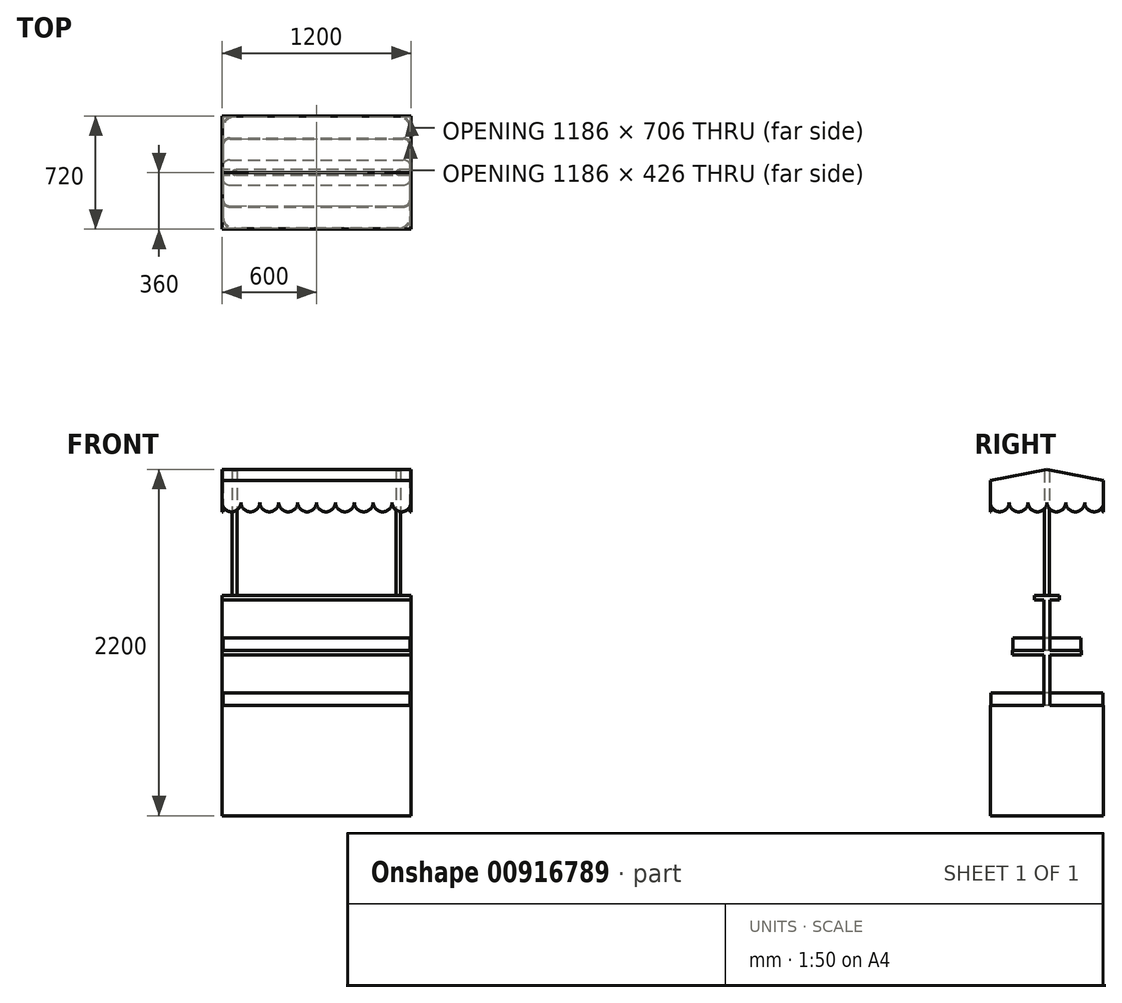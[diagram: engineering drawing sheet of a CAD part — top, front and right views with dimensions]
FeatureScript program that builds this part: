
annotation { "Feature Type Name" : "Feature", "Feature Type Description" : "" }
export const myFeature = defineFeature(function(context is Context, id is Id, definition is map)
    precondition{}
    {
        {
            var Q0;
            Q0=qCreatedBy(makeId("Front.planeOp"),FACE);
            var sketch = newSketch(context, id + "F0", { "sketchPlane" : qUnion([Q0])});
            skLineSegment(sketch, "E0.bottom", {"start": v(-600, 0) * mm, "end": v(600, 0) * mm});
            skLineSegment(sketch, "E0.top", {"start": v(-600, 1400) * mm, "end": v(600, 1400) * mm});
            skLineSegment(sketch, "E0.left", {"start": v(-600, 0) * mm, "end": v(-600, 1400) * mm});
            skLineSegment(sketch, "E0.right", {"start": v(600, 0) * mm, "end": v(600, 1400) * mm});
            skLineSegment(sketch, "E1", {"start": v(-600, 150) * mm, "end": v(600, 150) * mm});
            skLineSegment(sketch, "E2", {"start": v(-600, 700) * mm, "end": v(600, 700) * mm});
            skLineSegment(sketch, "E3", {"start": v(-600, 1370) * mm, "end": v(600, 1370) * mm});
            skLineSegment(sketch, "E4", {"start": v(-600, 1020) * mm, "end": v(600, 1020) * mm});
            skLineSegment(sketch, "E5", {"start": v(-600, 1050) * mm, "end": v(600, 1050) * mm});
            skSolve(sketch);
        }
        {
            var Q0;
            Q0=qCreatedBy(makeId("Top.planeOp"),FACE);
            var sketch = newSketch(context, id + "F1", { "sketchPlane" : qUnion([Q0])});
            skLineSegment(sketch, "E6.bottom", {"start": v(600, 360) * mm, "end": v(-600, 360) * mm});
            skLineSegment(sketch, "E6.top", {"start": v(600, -360) * mm, "end": v(-600, -360) * mm});
            skLineSegment(sketch, "E6.left", {"start": v(600, 360) * mm, "end": v(600, -360) * mm});
            skLineSegment(sketch, "E6.right", {"start": v(-600, 360) * mm, "end": v(-600, -360) * mm});
            skPoint(sketch, "E6.middle", {"position": v(0, 0) * mm});
            skLineSegment(sketch, "E7.bottom", {"start": v(600, 20) * mm, "end": v(-600, 20) * mm});
            skLineSegment(sketch, "E7.top", {"start": v(600, -20) * mm, "end": v(-600, -20) * mm});
            skLineSegment(sketch, "E7.left", {"start": v(600, 20) * mm, "end": v(600, -20) * mm});
            skLineSegment(sketch, "E7.right", {"start": v(-600, 20) * mm, "end": v(-600, -20) * mm});
            skLineSegment(sketch, "E8", {"start": v(-600, 220) * mm, "end": v(600, 220) * mm});
            skLineSegment(sketch, "E9", {"start": v(-600, -220) * mm, "end": v(600, -220) * mm});
            skLineSegment(sketch, "E10.0", {"start": v(550, 310) * mm, "end": v(-550, 310) * mm});
            skLineSegment(sketch, "E10.1", {"start": v(550, 310) * mm, "end": v(550, -310) * mm});
            skLineSegment(sketch, "E10.2", {"start": v(550, -310) * mm, "end": v(-550, -310) * mm});
            skLineSegment(sketch, "E10.3", {"start": v(-550, 310) * mm, "end": v(-550, -310) * mm});
            skLineSegment(sketch, "E11", {"start": v(-600, -80) * mm, "end": v(600, -80) * mm});
            skLineSegment(sketch, "E12", {"start": v(-600, 80) * mm, "end": v(600, 80) * mm});
            skSolve(sketch);
        }
        {
            var Q0;
            Q0=qCreatedBy(makeId("Top.planeOp"),FACE);
            var sketch = newSketch(context, id + "F2", { "sketchPlane" : qUnion([Q0])});
            skLineSegment(sketch, "E13.0", {"start": v(550, 310) * mm, "end": v(-550, 310) * mm});
            skLineSegment(sketch, "E13.1", {"start": v(-550, 310) * mm, "end": v(-550, -310) * mm});
            skLineSegment(sketch, "E13.2", {"start": v(550, -310) * mm, "end": v(-550, -310) * mm});
            skLineSegment(sketch, "E13.3", {"start": v(550, 310) * mm, "end": v(550, -310) * mm});
            skSolve(sketch);
        }
        {
            var Q0;
            Q0=qSketchRegion(id+"F2",true);
            var Q1;
            Q1=sQuery(id+"F0.wireOp",VERTEX,"E1.end");
            extrude(context, id + "F3", {"entities" : qUnion([Q0]), "endBound" : BoundingType.UP_TO_VERTEX, "depth" : 25 * mm, "endBoundEntityVertex" : qUnion([Q1]), "offsetDistance" : 25 * mm});
        }
        {
            var Q0;
            Q0=makeQuery(id+"F3.opExtrude","CAP_FACE",FACE,{"disambiguationData":[OSD([sQuery(id+"F2.wireOp",EDGE,"E13.0"),sQuery(id+"F2.wireOp",EDGE,"E13.1"),sQuery(id+"F2.wireOp",EDGE,"E13.2"),sQuery(id+"F2.wireOp",EDGE,"E13.3")])],"isStart":false});
            var sketch = newSketch(context, id + "F4", { "sketchPlane" : qUnion([Q0])});
            skLineSegment(sketch, "E14.0", {"start": v(600, 360) * mm, "end": v(-600, 360) * mm});
            skLineSegment(sketch, "E14.1", {"start": v(-600, 360) * mm, "end": v(-600, -360) * mm});
            skLineSegment(sketch, "E14.2", {"start": v(600, -360) * mm, "end": v(-600, -360) * mm});
            skLineSegment(sketch, "E14.3", {"start": v(600, 360) * mm, "end": v(600, -360) * mm});
            skSolve(sketch);
        }
        {
            var Q0;
            Q0=qSketchRegion(id+"F4",true);
            var Q1;
            Q1=sQuery(id+"F0.wireOp",VERTEX,"E2.end");
            extrude(context, id + "F5", {"entities" : qUnion([Q0]), "operationType" : NewBodyOperationType.ADD, "endBound" : BoundingType.UP_TO_VERTEX, "depth" : 25 * mm, "endBoundEntityVertex" : qUnion([Q1]), "offsetDistance" : 25 * mm});
        }
        {
            var Q0;
            Q0=makeQuery(id+"F5.opExtrude","CAP_FACE",FACE,{"disambiguationData":[OSD([sQuery(id+"F4.wireOp",EDGE,"E14.0"),sQuery(id+"F4.wireOp",EDGE,"E14.1"),sQuery(id+"F4.wireOp",EDGE,"E14.2"),sQuery(id+"F4.wireOp",EDGE,"E14.3")])],"isStart":false});
            var sketch = newSketch(context, id + "F6", { "sketchPlane" : qUnion([Q0])});
            skLineSegment(sketch, "E15.0", {"start": v(600, 20) * mm, "end": v(-600, 20) * mm});
            skLineSegment(sketch, "E15.1", {"start": v(600, -20) * mm, "end": v(-600, -20) * mm});
            skLineSegment(sketch, "E15.2", {"start": v(-600, 20) * mm, "end": v(-600, -20) * mm});
            skLineSegment(sketch, "E15.3", {"start": v(600, 20) * mm, "end": v(600, -20) * mm});
            skPoint(sketch, "E16.orphan", {"position": v(-600, 360) * mm});
            skPoint(sketch, "E17.orphan", {"position": v(-600, -360) * mm});
            skPoint(sketch, "E18.orphan", {"position": v(600, 360) * mm});
            skPoint(sketch, "E19.orphan", {"position": v(600, -360) * mm});
            skSolve(sketch);
        }
        {
            var Q0;
            Q0=qSketchRegion(id+"F6",true);
            var Q1;
            Q1=sQuery(id+"F0.wireOp",VERTEX,"E0.top.start");
            extrude(context, id + "F7", {"entities" : qUnion([Q0]), "operationType" : NewBodyOperationType.ADD, "endBound" : BoundingType.UP_TO_VERTEX, "depth" : 25 * mm, "endBoundEntityVertex" : qUnion([Q1]), "offsetDistance" : 25 * mm});
        }
        {
            var Q0;
            Q0=qCreatedBy(makeId("Top.planeOp"),FACE);
            var Q1;
            Q1=sQuery(id+"F0.wireOp",VERTEX,"E4.start");
            cPlane(context, id + "F8", {"entities" : qUnion([Q0, Q1]), "cplaneType" : CPlaneType.PLANE_POINT, "offset" : 25 * mm, "width" : 150 * mm, "height" : 150 * mm});
        }
        {
            var Q0;
            Q0=qCreatedBy(id+"F8.planeOp",FACE);
            var sketch = newSketch(context, id + "F9", { "sketchPlane" : qUnion([Q0])});
            skLineSegment(sketch, "E20.0", {"start": v(-600, 220) * mm, "end": v(600, 220) * mm});
            skLineSegment(sketch, "E20.1", {"start": v(-600, -220) * mm, "end": v(600, -220) * mm});
            skLineSegment(sketch, "E21", {"start": v(-600, 220) * mm, "end": v(-600, -220) * mm});
            skLineSegment(sketch, "E22", {"start": v(600, -220) * mm, "end": v(600, 220) * mm});
            skSolve(sketch);
        }
        {
            var Q0;
            Q0=qSketchRegion(id+"F9",true);
            var Q1;
            Q1=sQuery(id+"F0.wireOp",VERTEX,"E5.start");
            extrude(context, id + "F10", {"entities" : qUnion([Q0]), "operationType" : NewBodyOperationType.ADD, "endBound" : BoundingType.UP_TO_VERTEX, "depth" : 25 * mm, "endBoundEntityVertex" : qUnion([Q1]), "offsetDistance" : 25 * mm});
        }
        {
            var Q0;
            Q0=makeQuery(id+"F7.opExtrude","CAP_FACE",FACE,{"disambiguationData":[OSD([sQuery(id+"F6.wireOp",EDGE,"E15.0"),sQuery(id+"F6.wireOp",EDGE,"E15.1"),sQuery(id+"F6.wireOp",EDGE,"E15.2"),sQuery(id+"F6.wireOp",EDGE,"E15.3")])],"isStart":false});
            var sketch = newSketch(context, id + "F11", { "sketchPlane" : qUnion([Q0])});
            skLineSegment(sketch, "E23.0", {"start": v(-600, -80) * mm, "end": v(600, -80) * mm});
            skLineSegment(sketch, "E23.1", {"start": v(-600, 80) * mm, "end": v(600, 80) * mm});
            skLineSegment(sketch, "E24", {"start": v(-600, -80) * mm, "end": v(-600, 80) * mm});
            skLineSegment(sketch, "E25", {"start": v(600, -80) * mm, "end": v(600, 80) * mm});
            skSolve(sketch);
        }
        {
            var Q0;
            Q0=qSketchRegion(id+"F11",true);
            var Q1;
            Q1=sQuery(id+"F0.wireOp",VERTEX,"E3.start");
            extrude(context, id + "F12", {"entities" : qUnion([Q0]), "operationType" : NewBodyOperationType.ADD, "endBound" : BoundingType.UP_TO_VERTEX, "oppositeDirection" : true, "depth" : 25 * mm, "endBoundEntityVertex" : qUnion([Q1]), "offsetDistance" : 25 * mm});
        }
        {
            var Q0;
            Q0=makeQuery(id+"F5.opExtrude","SWEPT_EDGE",EDGE,{"disambiguationData":[OSD([sQuery(id+"F4.wireOp",EDGE,"E14.2"),sQuery(id+"F4.wireOp",EDGE,"E14.3")])]});
            var Q1;
            Q1=makeQuery(id+"F5.opExtrude","SWEPT_EDGE",EDGE,{"disambiguationData":[OSD([sQuery(id+"F4.wireOp",EDGE,"E14.1"),sQuery(id+"F4.wireOp",EDGE,"E14.2")])]});
            var Q2;
            Q2=makeQuery(id+"F5.opExtrude","SWEPT_EDGE",EDGE,{"disambiguationData":[OSD([sQuery(id+"F4.wireOp",EDGE,"E14.0"),sQuery(id+"F4.wireOp",EDGE,"E14.3")])]});
            var Q3;
            Q3=makeQuery(id+"F5.opExtrude","SWEPT_EDGE",EDGE,{"disambiguationData":[OSD([sQuery(id+"F4.wireOp",EDGE,"E14.0"),sQuery(id+"F4.wireOp",EDGE,"E14.1")])]});
            fillet(context, id + "F13", {"entities" : qUnion([Q0, Q1, Q2, Q3]), "radius" : 80 * mm, "tangentPropagation" : true, "allowEdgeOverflow" : false});
        }
        {
            var Q0;
            Q0=makeQuery(id+"F3.opExtrude","SWEPT_EDGE",EDGE,{"disambiguationData":[OSD([sQuery(id+"F2.wireOp",EDGE,"E13.0"),sQuery(id+"F2.wireOp",EDGE,"E13.1")])]});
            var Q1;
            Q1=makeQuery(id+"F3.opExtrude","SWEPT_EDGE",EDGE,{"disambiguationData":[OSD([sQuery(id+"F2.wireOp",EDGE,"E13.1"),sQuery(id+"F2.wireOp",EDGE,"E13.2")])]});
            var Q2;
            Q2=makeQuery(id+"F3.opExtrude","SWEPT_EDGE",EDGE,{"disambiguationData":[OSD([sQuery(id+"F2.wireOp",EDGE,"E13.2"),sQuery(id+"F2.wireOp",EDGE,"E13.3")])]});
            var Q3;
            Q3=makeQuery(id+"F3.opExtrude","SWEPT_EDGE",EDGE,{"disambiguationData":[OSD([sQuery(id+"F2.wireOp",EDGE,"E13.0"),sQuery(id+"F2.wireOp",EDGE,"E13.3")])]});
            fillet(context, id + "F14", {"entities" : qUnion([Q0, Q1, Q2, Q3]), "radius" : 85 * mm, "tangentPropagation" : true, "allowEdgeOverflow" : false});
        }
        {
            var Q0;
            Q0=makeQuery(id+"F10.opExtrude","SWEPT_EDGE",EDGE,{"disambiguationData":[OSD([sQuery(id+"F9.wireOp",EDGE,"E20.0"),sQuery(id+"F9.wireOp",EDGE,"E22")])]});
            var Q1;
            Q1=makeQuery(id+"F10.opExtrude","SWEPT_EDGE",EDGE,{"disambiguationData":[OSD([sQuery(id+"F9.wireOp",EDGE,"E20.0"),sQuery(id+"F9.wireOp",EDGE,"E21")])]});
            var Q2;
            Q2=makeQuery(id+"F10.opExtrude","SWEPT_EDGE",EDGE,{"disambiguationData":[OSD([sQuery(id+"F9.wireOp",EDGE,"E20.1"),sQuery(id+"F9.wireOp",EDGE,"E21")])]});
            var Q3;
            Q3=makeQuery(id+"F10.opExtrude","SWEPT_EDGE",EDGE,{"disambiguationData":[OSD([sQuery(id+"F9.wireOp",EDGE,"E20.1"),sQuery(id+"F9.wireOp",EDGE,"E22")])]});
            fillet(context, id + "F15", {"entities" : qUnion([Q0, Q1, Q2, Q3]), "radius" : 50 * mm, "tangentPropagation" : true, "allowEdgeOverflow" : false});
        }
        {
            var Q0;
            Q0=makeQuery(id+"F12.opExtrude","SWEPT_EDGE",EDGE,{"disambiguationData":[OSD([sQuery(id+"F11.wireOp",EDGE,"E23.0"),sQuery(id+"F11.wireOp",EDGE,"E25")])]});
            var Q1;
            Q1=makeQuery(id+"F12.opExtrude","SWEPT_EDGE",EDGE,{"disambiguationData":[OSD([sQuery(id+"F11.wireOp",EDGE,"E23.1"),sQuery(id+"F11.wireOp",EDGE,"E25")])]});
            var Q2;
            Q2=makeQuery(id+"F12.opExtrude","SWEPT_EDGE",EDGE,{"disambiguationData":[OSD([sQuery(id+"F11.wireOp",EDGE,"E23.0"),sQuery(id+"F11.wireOp",EDGE,"E24")])]});
            var Q3;
            Q3=makeQuery(id+"F12.opExtrude","SWEPT_EDGE",EDGE,{"disambiguationData":[OSD([sQuery(id+"F11.wireOp",EDGE,"E23.1"),sQuery(id+"F11.wireOp",EDGE,"E24")])]});
            fillet(context, id + "F16", {"entities" : qUnion([Q0, Q1, Q2, Q3]), "radius" : 50 * mm, "tangentPropagation" : true, "allowEdgeOverflow" : false});
        }
        {
            var Q0;
            {var subQ0=sQuery(id+"F4.wireOp",EDGE,"E14.3");var subQ1=sQuery(id+"F4.wireOp",EDGE,"E14.2");var subQ2=sQuery(id+"F4.wireOp",EDGE,"E14.1");Q0=makeQuery(id+"F7.boolean.opBoolean","SPLIT",FACE,{"disambiguationData":[TD([makeQuery(id+"F5.opExtrude","SWEPT_FACE",FACE,{"disambiguationData":[OSD([subQ1])]})])],"derivedFrom":makeQuery(id+"F5.opExtrude","CAP_FACE",FACE,{"disambiguationData":[OSD([sQuery(id+"F4.wireOp",EDGE,"E14.0"),subQ2,subQ1,subQ0])],"isStart":false})});}
            var sketch = newSketch(context, id + "F17", { "sketchPlane" : qUnion([Q0])});
            skArc(sketch, "E26.0", {"start": v(-595, 280) * mm, "mid": v(-573.03, 333.03) * mm, "end": v(-520, 355) * mm});
            skLineSegment(sketch, "E26.1", {"start": v(520, 355) * mm, "end": v(-520, 355) * mm});
            skLineSegment(sketch, "E26.2", {"start": v(-595, 280) * mm, "end": v(-595, -280) * mm});
            skArc(sketch, "E26.3", {"start": v(520, 355) * mm, "mid": v(573.03, 333.03) * mm, "end": v(595, 280) * mm});
            skArc(sketch, "E26.4", {"start": v(-520, -355) * mm, "mid": v(-573.03, -333.03) * mm, "end": v(-595, -280) * mm});
            skLineSegment(sketch, "E26.5", {"start": v(520, -355) * mm, "end": v(-520, -355) * mm});
            skArc(sketch, "E26.6", {"start": v(595, -280) * mm, "mid": v(573.03, -333.03) * mm, "end": v(520, -355) * mm});
            skLineSegment(sketch, "E26.7", {"start": v(595, 280) * mm, "end": v(595, -280) * mm});
            skLineSegment(sketch, "E27.0", {"start": v(520, -353) * mm, "end": v(-520, -353) * mm});
            skArc(sketch, "E27.1", {"start": v(593, -280) * mm, "mid": v(571.62, -331.62) * mm, "end": v(520, -353) * mm});
            skArc(sketch, "E27.2", {"start": v(-520, -353) * mm, "mid": v(-571.62, -331.62) * mm, "end": v(-593, -280) * mm});
            skLineSegment(sketch, "E27.3", {"start": v(593, 280) * mm, "end": v(593, -280) * mm});
            skLineSegment(sketch, "E27.4", {"start": v(-593, 280) * mm, "end": v(-593, -280) * mm});
            skArc(sketch, "E27.5", {"start": v(-593, 280) * mm, "mid": v(-571.62, 331.62) * mm, "end": v(-520, 353) * mm});
            skLineSegment(sketch, "E27.6", {"start": v(520, 353) * mm, "end": v(-520, 353) * mm});
            skArc(sketch, "E27.7", {"start": v(520, 353) * mm, "mid": v(571.62, 331.62) * mm, "end": v(593, 280) * mm});
            skSolve(sketch);
        }
        {
            var Q0;
            Q0=qSketchRegion(id+"F17",true);
            extrude(context, id + "F18", {"entities" : qUnion([Q0]), "depth" : 80 * mm, "offsetDistance" : 25 * mm});
        }
        {
            var Q0;
            {var subQ0=sQuery(id+"F9.wireOp",EDGE,"E20.1");var subQ1=sQuery(id+"F9.wireOp",EDGE,"E21");var subQ2=sQuery(id+"F9.wireOp",EDGE,"E22");Q0=makeQuery(id+"F10.boolean.opBoolean","SPLIT",FACE,{"disambiguationData":[TD([makeQuery(id+"F7.opExtrude","SWEPT_FACE",FACE,{"disambiguationData":[OSD([sQuery(id+"F6.wireOp",EDGE,"E15.1")])]})])],"derivedFrom":makeQuery(id+"F10.opExtrude","CAP_FACE",FACE,{"disambiguationData":[OSD([sQuery(id+"F9.wireOp",EDGE,"E20.0"),subQ0,subQ1,subQ2])],"isStart":false})});}
            var sketch = newSketch(context, id + "F19", { "sketchPlane" : qUnion([Q0])});
            skLineSegment(sketch, "E28.0", {"start": v(-595, 170) * mm, "end": v(-595, 15) * mm});
            skLineSegment(sketch, "E28.1", {"start": v(595, 15) * mm, "end": v(595, 170) * mm});
            skArc(sketch, "E28.2", {"start": v(595, 170) * mm, "mid": v(581.82, 201.82) * mm, "end": v(550, 215) * mm});
            skLineSegment(sketch, "E28.3", {"start": v(-550, 215) * mm, "end": v(550, 215) * mm});
            skArc(sketch, "E28.4", {"start": v(-550, 215) * mm, "mid": v(-581.82, 201.82) * mm, "end": v(-595, 170) * mm});
            skLineSegment(sketch, "E29.0", {"start": v(595, -170) * mm, "end": v(595, -15) * mm});
            skLineSegment(sketch, "E29.1", {"start": v(-595, -15) * mm, "end": v(-595, -170) * mm});
            skArc(sketch, "E29.2", {"start": v(-595, -170) * mm, "mid": v(-581.82, -201.82) * mm, "end": v(-550, -215) * mm});
            skLineSegment(sketch, "E29.3", {"start": v(-550, -215) * mm, "end": v(550, -215) * mm});
            skArc(sketch, "E29.4", {"start": v(550, -215) * mm, "mid": v(581.82, -201.82) * mm, "end": v(595, -170) * mm});
            skLineSegment(sketch, "E30", {"start": v(-595, 15) * mm, "end": v(-595, -15) * mm});
            skLineSegment(sketch, "E31", {"start": v(595, 15) * mm, "end": v(595, -15) * mm});
            skLineSegment(sketch, "E32.0", {"start": v(593, 15) * mm, "end": v(593, 170) * mm});
            skLineSegment(sketch, "E32.1", {"start": v(-593, 15) * mm, "end": v(-593, -15) * mm});
            skLineSegment(sketch, "E32.2", {"start": v(-593, 170) * mm, "end": v(-593, 15) * mm});
            skArc(sketch, "E32.3", {"start": v(-550, 213) * mm, "mid": v(-580.4, 200.4) * mm, "end": v(-593, 170) * mm});
            skLineSegment(sketch, "E32.4", {"start": v(-550, 213) * mm, "end": v(550, 213) * mm});
            skLineSegment(sketch, "E32.5", {"start": v(-593, -15) * mm, "end": v(-593, -170) * mm});
            skArc(sketch, "E32.6", {"start": v(593, 170) * mm, "mid": v(580.4, 200.4) * mm, "end": v(550, 213) * mm});
            skArc(sketch, "E32.7", {"start": v(-593, -170) * mm, "mid": v(-580.4, -200.4) * mm, "end": v(-550, -213) * mm});
            skLineSegment(sketch, "E32.8", {"start": v(-550, -213) * mm, "end": v(550, -213) * mm});
            skArc(sketch, "E32.9", {"start": v(550, -213) * mm, "mid": v(580.4, -200.4) * mm, "end": v(593, -170) * mm});
            skLineSegment(sketch, "E32.10", {"start": v(593, -170) * mm, "end": v(593, -15) * mm});
            skLineSegment(sketch, "E32.11", {"start": v(593, 15) * mm, "end": v(593, -15) * mm});
            skSolve(sketch);
        }
        {
            var Q0;
            Q0=qSketchRegion(id+"F19",true);
            extrude(context, id + "F20", {"entities" : qUnion([Q0]), "depth" : 80 * mm, "offsetDistance" : 25 * mm});
        }
        {
            var Q0;
            Q0=makeQuery(id+"F12.boolean.opBoolean","MERGE",FACE,{"derivedFrom":[makeQuery(id+"F10.boolean.opBoolean","MERGE",FACE,{"derivedFrom":[makeQuery(id+"F7.boolean.opBoolean","MERGE",FACE,{"derivedFrom":[makeQuery(id+"F5.opExtrude","SWEPT_FACE",FACE,{"disambiguationData":[OSD([sQuery(id+"F4.wireOp",EDGE,"E14.3")])]}),makeQuery(id+"F7.opExtrude","SWEPT_FACE",FACE,{"disambiguationData":[OSD([sQuery(id+"F6.wireOp",EDGE,"E15.3")])]})]}),makeQuery(id+"F10.opExtrude","SWEPT_FACE",FACE,{"disambiguationData":[OSD([sQuery(id+"F9.wireOp",EDGE,"E22")])]})]}),makeQuery(id+"F12.opExtrude","SWEPT_FACE",FACE,{"disambiguationData":[OSD([sQuery(id+"F11.wireOp",EDGE,"E25")])]})]});
            var sketch = newSketch(context, id + "F21", { "sketchPlane" : qUnion([Q0])});
            skLineSegment(sketch, "E33", {"start": v(0, 0) * mm, "end": v(0, 2200) * mm, "construction": true});
            skLineSegment(sketch, "E34", {"start": v(0, 2200) * mm, "end": v(-360, 2130) * mm});
            skLineSegment(sketch, "E35", {"start": v(-360, 2130) * mm, "end": v(-360, 1930) * mm});
            skLineSegment(sketch, "E36.MirrorCS", {"start": v(0, 2200) * mm, "end": v(360, 2130) * mm});
            skLineSegment(sketch, "E37.MirrorCS", {"start": v(360, 2130) * mm, "end": v(360, 1930) * mm});
            skSolve(sketch);
        }
        {
            var Q0;
            {var subQ6=sQuery(id+"F4.wireOp",EDGE,"E14.3");Q0=makeQuery(id+"F21.imprint","IMPRINT",FACE,{"disambiguationData":[TD([[makeQuery(id+"F21.imprint","IMPRINT",EDGE,{"derivedFrom":makeQuery(id+"F5.opExtrude","CAP_EDGE",EDGE,{"disambiguationData":[OSD([subQ6])],"isStart":true})}),-1.0]])]});}
            var sketch = newSketch(context, id + "F22", { "sketchPlane" : qUnion([Q0])});
            skLineSegment(sketch, "E38.0", {"start": v(0, 2200) * mm, "end": v(-360, 2130) * mm});
            skLineSegment(sketch, "E38.1", {"start": v(0, 2200) * mm, "end": v(360, 2130) * mm});
            skLineSegment(sketch, "E39.0", {"start": v(0, 2194.9) * mm, "end": v(-359.3, 2125.04) * mm});
            skLineSegment(sketch, "E39.1", {"start": v(0, 2194.9) * mm, "end": v(359.3, 2125.04) * mm});
            skLineSegment(sketch, "E40", {"start": v(-360, 2130) * mm, "end": v(-359.3, 2125.04) * mm});
            skLineSegment(sketch, "E41", {"start": v(359.3, 2125.04) * mm, "end": v(360, 2130) * mm});
            skSolve(sketch);
        }
        {
            var Q0;
            Q0 = qSketchRegion(id + "F22", true);
            var Q1;
            Q1=makeQuery(id+"F12.boolean.opBoolean","MERGE",FACE,{"derivedFrom":[makeQuery(id+"F10.boolean.opBoolean","MERGE",FACE,{"derivedFrom":[makeQuery(id+"F7.boolean.opBoolean","MERGE",FACE,{"derivedFrom":[makeQuery(id+"F5.opExtrude","SWEPT_FACE",FACE,{"disambiguationData":[OSD([sQuery(id+"F4.wireOp",EDGE,"E14.1")])]}),makeQuery(id+"F7.opExtrude","SWEPT_FACE",FACE,{"disambiguationData":[OSD([sQuery(id+"F6.wireOp",EDGE,"E15.2")])]})]}),makeQuery(id+"F10.opExtrude","SWEPT_FACE",FACE,{"disambiguationData":[OSD([sQuery(id+"F9.wireOp",EDGE,"E21")])]})]}),makeQuery(id+"F12.opExtrude","SWEPT_FACE",FACE,{"disambiguationData":[OSD([sQuery(id+"F11.wireOp",EDGE,"E24")])]})]});
            extrude(context, id + "F23", {"entities" : qUnion([Q0]), "endBound" : BoundingType.UP_TO_SURFACE, "oppositeDirection" : true, "depth" : 2960 * mm, "endBoundEntityFace" : qUnion([Q1]), "offsetDistance" : 25 * mm});
        }
        {
            var Q0;
            Q0=makeQuery(id+"F5.opExtrude","SWEPT_FACE",FACE,{"disambiguationData":[OSD([sQuery(id+"F4.wireOp",EDGE,"E14.2")])]});
            var sketch = newSketch(context, id + "F24", { "sketchPlane" : qUnion([Q0])});
            skLineSegment(sketch, "E42.0", {"start": v(-600, 2130) * mm, "end": v(600, 2130) * mm});
            skLineSegment(sketch, "E43", {"start": v(-600, 2130) * mm, "end": v(-600, 1990) * mm});
            skArc(sketch, "E44", {"start": v(-600, 1990) * mm, "mid": v(-540, 1930) * mm, "end": v(-480, 1990) * mm});
            skArc(sketch, "E45.1.0.0", {"start": v(-480, 1990) * mm, "mid": v(-420, 1930) * mm, "end": v(-360, 1990) * mm});
            skArc(sketch, "E45.2.0.0", {"start": v(-360, 1990) * mm, "mid": v(-300, 1930) * mm, "end": v(-240, 1990) * mm});
            skArc(sketch, "E45.3.0.0", {"start": v(-240, 1990) * mm, "mid": v(-180, 1930) * mm, "end": v(-120, 1990) * mm});
            skArc(sketch, "E45.4.0.0", {"start": v(-120, 1990) * mm, "mid": v(-60, 1930) * mm, "end": v(0, 1990) * mm});
            skArc(sketch, "E45.5.0.0", {"start": v(0, 1990) * mm, "mid": v(60, 1930) * mm, "end": v(120, 1990) * mm});
            skArc(sketch, "E45.6.0.0", {"start": v(120, 1990) * mm, "mid": v(180, 1930) * mm, "end": v(240, 1990) * mm});
            skArc(sketch, "E45.7.0.0", {"start": v(240, 1990) * mm, "mid": v(300, 1930) * mm, "end": v(360, 1990) * mm});
            skArc(sketch, "E45.8.0.0", {"start": v(360, 1990) * mm, "mid": v(420, 1930) * mm, "end": v(480, 1990) * mm});
            skArc(sketch, "E45.9.0.0", {"start": v(480, 1990) * mm, "mid": v(540, 1930) * mm, "end": v(600, 1990) * mm});
            skLineSegment(sketch, "E45.direction1", {"start": v(-600, 1990) * mm, "end": v(-480, 1990) * mm, "construction": true});
            skLineSegment(sketch, "E46", {"start": v(600, 2130) * mm, "end": v(600, 1990) * mm});
            skSolve(sketch);
        }
        {
            var Q0;
            Q0 = qSketchRegion(id + "F24", true);
            extrude(context, id + "F25", {"entities" : qUnion([Q0]), "operationType" : NewBodyOperationType.ADD, "oppositeDirection" : true, "depth" : 5 * mm, "offsetDistance" : 25 * mm});
        }
        {
            var Q0;
            Q0=makeQuery(id+"F5.opExtrude","SWEPT_FACE",FACE,{"disambiguationData":[OSD([sQuery(id+"F4.wireOp",EDGE,"E14.0")])]});
            var sketch = newSketch(context, id + "F26", { "sketchPlane" : qUnion([Q0])});
            skLineSegment(sketch, "E47.0", {"start": v(600, 2130) * mm, "end": v(-600, 2130) * mm});
            skLineSegment(sketch, "E48", {"start": v(-600, 2130) * mm, "end": v(-600, 1990) * mm});
            skArc(sketch, "E49", {"start": v(-600, 1990) * mm, "mid": v(-540, 1930) * mm, "end": v(-480, 1990) * mm});
            skArc(sketch, "E50.1.0.0", {"start": v(-480, 1990) * mm, "mid": v(-420, 1930) * mm, "end": v(-360, 1990) * mm});
            skArc(sketch, "E50.2.0.0", {"start": v(-360, 1990) * mm, "mid": v(-300, 1930) * mm, "end": v(-240, 1990) * mm});
            skArc(sketch, "E50.3.0.0", {"start": v(-240, 1990) * mm, "mid": v(-180, 1930) * mm, "end": v(-120, 1990) * mm});
            skArc(sketch, "E50.4.0.0", {"start": v(-120, 1990) * mm, "mid": v(-60, 1930) * mm, "end": v(0, 1990) * mm});
            skArc(sketch, "E50.5.0.0", {"start": v(0, 1990) * mm, "mid": v(60, 1930) * mm, "end": v(120, 1990) * mm});
            skArc(sketch, "E50.6.0.0", {"start": v(120, 1990) * mm, "mid": v(180, 1930) * mm, "end": v(240, 1990) * mm});
            skArc(sketch, "E50.7.0.0", {"start": v(240, 1990) * mm, "mid": v(300, 1930) * mm, "end": v(360, 1990) * mm});
            skArc(sketch, "E50.8.0.0", {"start": v(360, 1990) * mm, "mid": v(420, 1930) * mm, "end": v(480, 1990) * mm});
            skArc(sketch, "E50.9.0.0", {"start": v(480, 1990) * mm, "mid": v(540, 1930) * mm, "end": v(600, 1990) * mm});
            skLineSegment(sketch, "E50.direction1", {"start": v(-600, 1990) * mm, "end": v(-480, 1990) * mm, "construction": true});
            skLineSegment(sketch, "E51", {"start": v(600, 2130) * mm, "end": v(600, 1990) * mm});
            skSolve(sketch);
        }
        {
            var Q0;
            Q0 = qSketchRegion(id + "F26", true);
            extrude(context, id + "F27", {"entities" : qUnion([Q0]), "operationType" : NewBodyOperationType.ADD, "oppositeDirection" : true, "depth" : 5 * mm, "offsetDistance" : 25 * mm});
        }
        {
            var Q0;
            Q0=makeQuery(id+"F12.boolean.opBoolean","MERGE",FACE,{"derivedFrom":[makeQuery(id+"F10.boolean.opBoolean","MERGE",FACE,{"derivedFrom":[makeQuery(id+"F7.boolean.opBoolean","MERGE",FACE,{"derivedFrom":[makeQuery(id+"F5.opExtrude","SWEPT_FACE",FACE,{"disambiguationData":[OSD([sQuery(id+"F4.wireOp",EDGE,"E14.3")])]}),makeQuery(id+"F7.opExtrude","SWEPT_FACE",FACE,{"disambiguationData":[OSD([sQuery(id+"F6.wireOp",EDGE,"E15.3")])]})]}),makeQuery(id+"F10.opExtrude","SWEPT_FACE",FACE,{"disambiguationData":[OSD([sQuery(id+"F9.wireOp",EDGE,"E22")])]})]}),makeQuery(id+"F12.opExtrude","SWEPT_FACE",FACE,{"disambiguationData":[OSD([sQuery(id+"F11.wireOp",EDGE,"E25")])]})]});
            var sketch = newSketch(context, id + "F28", { "sketchPlane" : qUnion([Q0])});
            skLineSegment(sketch, "E52.0", {"start": v(0, 2200) * mm, "end": v(-360, 2130) * mm});
            skLineSegment(sketch, "E52.1", {"start": v(-360, 1990) * mm, "end": v(-360, 2130) * mm});
            skArc(sketch, "E53", {"start": v(-360, 1990) * mm, "mid": v(-300, 1930) * mm, "end": v(-240, 1990) * mm});
            skArc(sketch, "E54.1.0.0", {"start": v(-240, 1990) * mm, "mid": v(-180, 1930) * mm, "end": v(-120, 1990) * mm});
            skArc(sketch, "E54.2.0.0", {"start": v(-120, 1990) * mm, "mid": v(-60, 1930) * mm, "end": v(0, 1990) * mm});
            skArc(sketch, "E54.3.0.0", {"start": v(0, 1990) * mm, "mid": v(60, 1930) * mm, "end": v(120, 1990) * mm});
            skArc(sketch, "E54.4.0.0", {"start": v(120, 1990) * mm, "mid": v(180, 1930) * mm, "end": v(240, 1990) * mm});
            skArc(sketch, "E54.5.0.0", {"start": v(240, 1990) * mm, "mid": v(300, 1930) * mm, "end": v(360, 1990) * mm});
            skLineSegment(sketch, "E54.direction1", {"start": v(-360, 1990) * mm, "end": v(-240, 1990) * mm, "construction": true});
            skLineSegment(sketch, "E55.1", {"start": v(0, 2200) * mm, "end": v(360, 2130) * mm});
            skLineSegment(sketch, "E56", {"start": v(360, 2130) * mm, "end": v(360, 1990) * mm});
            skSolve(sketch);
        }
        {
            var Q0;
            Q0=makeQuery(id+"F28.imprint","IMPRINT",FACE,{"disambiguationData":[TD([[makeQuery(id+"F28.imprint","IMPRINT",EDGE,{"derivedFrom":sQuery(id+"F28.wireOp",EDGE,"E52.0")}),1.0]])]});
            extrude(context, id + "F29", {"entities" : qUnion([Q0]), "operationType" : NewBodyOperationType.ADD, "oppositeDirection" : true, "depth" : 5 * mm, "offsetDistance" : 25 * mm});
        }
        {
            var Q0;
            Q0=makeQuery(id+"F12.boolean.opBoolean","MERGE",FACE,{"derivedFrom":[makeQuery(id+"F10.boolean.opBoolean","MERGE",FACE,{"derivedFrom":[makeQuery(id+"F7.boolean.opBoolean","MERGE",FACE,{"derivedFrom":[makeQuery(id+"F5.opExtrude","SWEPT_FACE",FACE,{"disambiguationData":[OSD([sQuery(id+"F4.wireOp",EDGE,"E14.1")])]}),makeQuery(id+"F7.opExtrude","SWEPT_FACE",FACE,{"disambiguationData":[OSD([sQuery(id+"F6.wireOp",EDGE,"E15.2")])]})]}),makeQuery(id+"F10.opExtrude","SWEPT_FACE",FACE,{"disambiguationData":[OSD([sQuery(id+"F9.wireOp",EDGE,"E21")])]})]}),makeQuery(id+"F12.opExtrude","SWEPT_FACE",FACE,{"disambiguationData":[OSD([sQuery(id+"F11.wireOp",EDGE,"E24")])]})]});
            var sketch = newSketch(context, id + "F30", { "sketchPlane" : qUnion([Q0])});
            skArc(sketch, "E57", {"start": v(-360, 1990) * mm, "mid": v(-300, 1930) * mm, "end": v(-240, 1990) * mm});
            skArc(sketch, "E58.1.0.0", {"start": v(-240, 1990) * mm, "mid": v(-180, 1930) * mm, "end": v(-120, 1990) * mm});
            skArc(sketch, "E58.2.0.0", {"start": v(-120, 1990) * mm, "mid": v(-60, 1930) * mm, "end": v(0, 1990) * mm});
            skArc(sketch, "E58.3.0.0", {"start": v(0, 1990) * mm, "mid": v(60, 1930) * mm, "end": v(120, 1990) * mm});
            skArc(sketch, "E58.4.0.0", {"start": v(120, 1990) * mm, "mid": v(180, 1930) * mm, "end": v(240, 1990) * mm});
            skArc(sketch, "E58.5.0.0", {"start": v(240, 1990) * mm, "mid": v(300, 1930) * mm, "end": v(360, 1990) * mm});
            skLineSegment(sketch, "E58.direction1", {"start": v(-360, 1990) * mm, "end": v(-240, 1990) * mm, "construction": true});
            skLineSegment(sketch, "E59.0", {"start": v(360, 2130) * mm, "end": v(0, 2200) * mm});
            skLineSegment(sketch, "E59.1", {"start": v(360, 2130) * mm, "end": v(360, 1990) * mm});
            skLineSegment(sketch, "E60.0", {"start": v(-360, 2130) * mm, "end": v(0, 2200) * mm});
            skLineSegment(sketch, "E60.1", {"start": v(-360, 2130) * mm, "end": v(-360, 1990) * mm});
            skSolve(sketch);
        }
        {
            var Q0;
            Q0 = qSketchRegion(id + "F30", true);
            extrude(context, id + "F31", {"entities" : qUnion([Q0]), "operationType" : NewBodyOperationType.ADD, "oppositeDirection" : true, "depth" : 5 * mm, "offsetDistance" : 25 * mm});
        }
        {
            var Q0;
            Q0=makeQuery(id+"F12.boolean.opBoolean","MERGE",FACE,{"derivedFrom":[makeQuery(id+"F7.opExtrude","CAP_FACE",FACE,{"disambiguationData":[OSD([sQuery(id+"F6.wireOp",EDGE,"E15.0"),sQuery(id+"F6.wireOp",EDGE,"E15.1"),sQuery(id+"F6.wireOp",EDGE,"E15.2"),sQuery(id+"F6.wireOp",EDGE,"E15.3")])],"isStart":false}),makeQuery(id+"F12.opExtrude","CAP_FACE",FACE,{"disambiguationData":[OSD([sQuery(id+"F11.wireOp",EDGE,"E23.0"),sQuery(id+"F11.wireOp",EDGE,"E23.1"),sQuery(id+"F11.wireOp",EDGE,"E24"),sQuery(id+"F11.wireOp",EDGE,"E25")])],"isStart":true})]});
            var sketch = newSketch(context, id + "F32", { "sketchPlane" : qUnion([Q0])});
            skCircle(sketch, "E61", {"center": v(-520, 0) * mm, "radius": 15 * mm});
            skLineSegment(sketch, "E62", {"start": v(0, 350.36) * mm, "end": v(0, -351.1) * mm, "construction": true});
            skCircle(sketch, "E63.MirrorC", {"center": v(520, 0) * mm, "radius": 15 * mm});
            skSolve(sketch);
        }
        {
            var Q0;
            Q0 = qSketchRegion(id + "F32", true);
            extrude(context, id + "F33", {"entities" : qUnion([Q0]), "endBound" : BoundingType.UP_TO_NEXT, "depth" : 25 * mm, "offsetDistance" : 25 * mm});
        }
        {
            var Q0;
            Q0=makeQuery(id+"F5.opExtrude","CAP_FACE",FACE,{"disambiguationData":[OSD([sQuery(id+"F4.wireOp",EDGE,"E14.0"),sQuery(id+"F4.wireOp",EDGE,"E14.1"),sQuery(id+"F4.wireOp",EDGE,"E14.2"),sQuery(id+"F4.wireOp",EDGE,"E14.3")])],"isStart":true});
            var sketch = newSketch(context, id + "F34", { "sketchPlane" : qUnion([Q0])});
            skArc(sketch, "E64.0", {"start": v(-520, 360) * mm, "mid": v(-576.57, 336.57) * mm, "end": v(-600, 280) * mm});
            skLineSegment(sketch, "E64.1", {"start": v(520, 360) * mm, "end": v(-520, 360) * mm});
            skArc(sketch, "E64.2", {"start": v(600, 280) * mm, "mid": v(576.57, 336.57) * mm, "end": v(520, 360) * mm});
            skLineSegment(sketch, "E64.3", {"start": v(600, -280) * mm, "end": v(600, 280) * mm});
            skArc(sketch, "E64.4", {"start": v(520, -360) * mm, "mid": v(576.57, -336.57) * mm, "end": v(600, -280) * mm});
            skLineSegment(sketch, "E64.5", {"start": v(520, -360) * mm, "end": v(-520, -360) * mm});
            skArc(sketch, "E64.6", {"start": v(-600, -280) * mm, "mid": v(-576.57, -336.57) * mm, "end": v(-520, -360) * mm});
            skLineSegment(sketch, "E64.7", {"start": v(-600, -280) * mm, "end": v(-600, 280) * mm});
            skSolve(sketch);
        }
        {
            var Q0;
            Q0 = qSketchRegion(id + "F34", true);
            var Q1;
            Q1=makeQuery(id+"F3.opExtrude","CAP_FACE",FACE,{"disambiguationData":[OSD([sQuery(id+"F2.wireOp",EDGE,"E13.0"),sQuery(id+"F2.wireOp",EDGE,"E13.1"),sQuery(id+"F2.wireOp",EDGE,"E13.2"),sQuery(id+"F2.wireOp",EDGE,"E13.3")])],"isStart":true});
            extrude(context, id + "F35", {"entities" : qUnion([Q0]), "operationType" : NewBodyOperationType.ADD, "endBound" : BoundingType.UP_TO_SURFACE, "depth" : 25 * mm, "endBoundEntityFace" : qUnion([Q1]), "offsetDistance" : 25 * mm});
        }
    });
